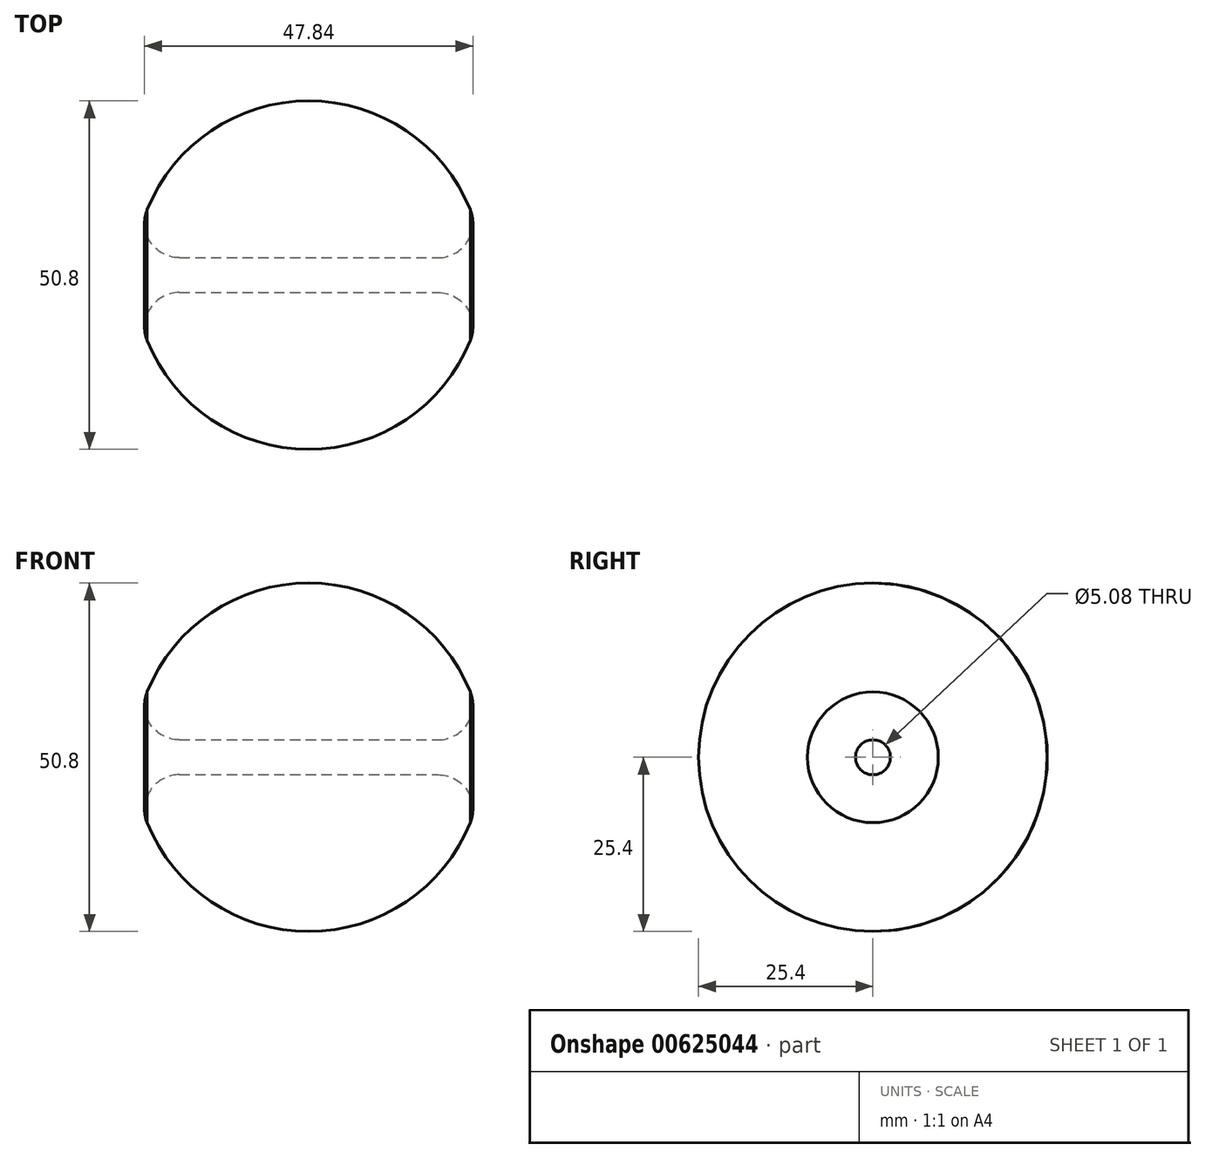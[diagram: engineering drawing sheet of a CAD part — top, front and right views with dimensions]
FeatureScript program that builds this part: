
annotation { "Feature Type Name" : "Feature", "Feature Type Description" : "" }
export const myFeature = defineFeature(function(context is Context, id is Id, definition is map)
    precondition{}
    {
        {
            var Q0;
            Q0=qCreatedBy(makeId("Front.planeOp"),FACE);
            var sketch = newSketch(context, id + "F0", { "sketchPlane" : qUnion([Q0])});
            skCircle(sketch, "E0", {"center": v(0, 0) * mm, "radius": 25.4 * mm});
            skSolve(sketch);
        }
        {
            var Q0;
            Q0=qCreatedBy(makeId("Top.planeOp"),FACE);
            var sketch = newSketch(context, id + "F1", { "sketchPlane" : qUnion([Q0])});
            skCircle(sketch, "E1", {"center": v(0, 0) * mm, "radius": 25.4 * mm});
            skSolve(sketch);
        }
        {
            var Q0;
            Q0=makeQuery(id+"F0.imprint","IMPRINT",FACE,{"disambiguationData":[TD([[makeQuery(id+"F0.imprint","IMPRINT",EDGE,{"derivedFrom":sQuery(id+"F0.wireOp",EDGE,"E0")}),1.0]])]});
            var Q1;
            Q1=sQuery(id+"F1.wireOp",EDGE,"E1");
            sweep(context, id + "F2", {"profiles" : qUnion([Q0]), "path" : qUnion([Q1])});
        }
        {
            var Q0;
            Q0=qCreatedBy(makeId("Right.planeOp"),FACE);
            cPlane(context, id + "F3", {"entities" : qUnion([Q0]), "cplaneType" : CPlaneType.OFFSET, "offset" : 26.67 * mm, "width" : 152.4 * mm, "height" : 152.4 * mm});
        }
        {
            var Q0;
            Q0=qCreatedBy(id+"F3.planeOp",FACE);
            var sketch = newSketch(context, id + "F4", { "sketchPlane" : qUnion([Q0])});
            skCircle(sketch, "E2", {"center": v(0, 0) * mm, "radius": 2.54 * mm});
            skSolve(sketch);
        }
        {
            var Q0;
            Q0=makeQuery(id+"F4.imprint","IMPRINT",FACE,{"disambiguationData":[TD([[makeQuery(id+"F4.imprint","IMPRINT",EDGE,{"derivedFrom":sQuery(id+"F4.wireOp",EDGE,"E2")}),1.0]])]});
            var Q1;
            Q1=sQuery(id+"F4.wireOp",EDGE,"E2");
            extrude(context, id + "F5", {"entities" : qUnion([Q0]), "operationType" : NewBodyOperationType.REMOVE, "surfaceEntities" : qUnion([Q1]), "oppositeDirection" : true, "depth" : 69.85 * mm, "offsetDistance" : 25.4 * mm});
        }
        {
            var Q0;
            Q0=makeQuery(id+"F5.boolean.opBoolean","INTERSECT",EDGE,{"disambiguationData":[OD(1.0)],"derivedFrom":[makeQuery(id+"F2.opSweep","SWEPT_FACE",FACE,{"disambiguationData":[OSD([sQuery(id+"F0.wireOp",EDGE,"E0"),sQuery(id+"F1.wireOp",EDGE,"E1")])]}),makeQuery(id+"F5.opExtrude","SWEPT_FACE",FACE,{"disambiguationData":[OSD([sQuery(id+"F4.wireOp",EDGE,"E2")])]})]});
            var Q1;
            Q1=makeQuery(id+"F5.boolean.opBoolean","INTERSECT",EDGE,{"disambiguationData":[OD(0.0)],"derivedFrom":[makeQuery(id+"F2.opSweep","SWEPT_FACE",FACE,{"disambiguationData":[OSD([sQuery(id+"F0.wireOp",EDGE,"E0"),sQuery(id+"F1.wireOp",EDGE,"E1")])]}),makeQuery(id+"F5.opExtrude","SWEPT_FACE",FACE,{"disambiguationData":[OSD([sQuery(id+"F4.wireOp",EDGE,"E2")])]})]});
            fillet(context, id + "F6", {"entities" : qUnion([Q0, Q1]), "radius" : 5.08 * mm, "tangentPropagation" : true, "allowEdgeOverflow" : false});
        }
    });
